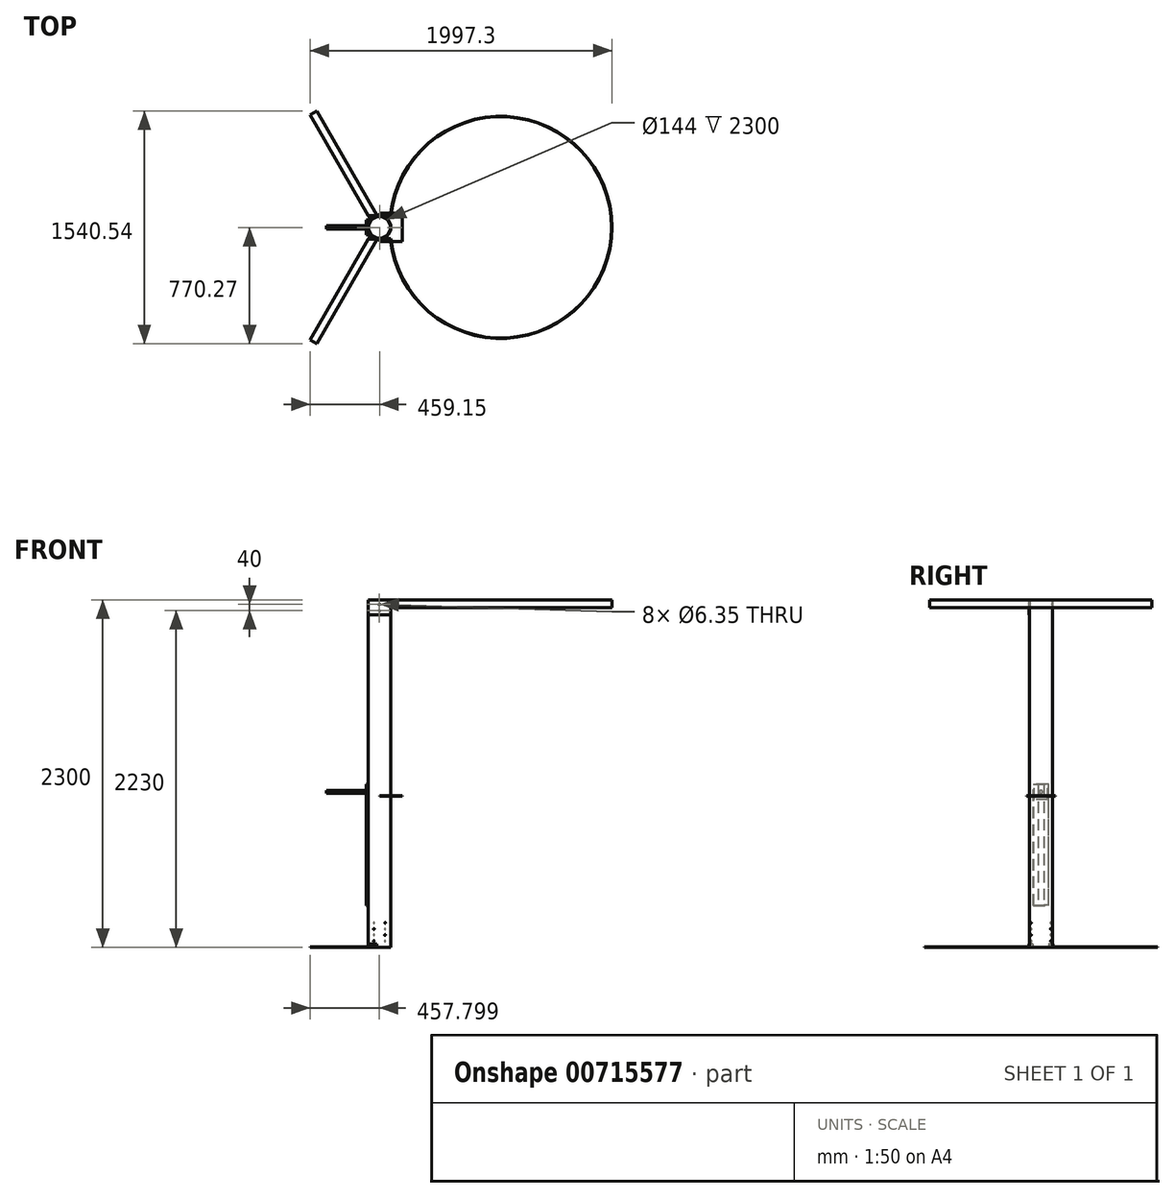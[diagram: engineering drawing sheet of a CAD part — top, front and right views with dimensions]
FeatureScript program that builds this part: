
annotation { "Feature Type Name" : "Feature", "Feature Type Description" : "" }
export const myFeature = defineFeature(function(context is Context, id is Id, definition is map)
    precondition{}
    {
        {
            assignVariable(context, id + "F0", {"name" : "DTubo", "anyValue" : 150 * mm});
        }
        {
            assignVariable(context, id + "F1", {"name" : "hTubo", "anyValue" : 2300 * mm});
        }
        {
            assignVariable(context, id + "F2", {"name" : "tSolera", "anyValue" : 3 * mm});
        }
        {
            assignVariable(context, id + "F3", {"name" : "hProl", "anyValue" : 20});
        }
        {
            assignVariable(context, id + "F4", {"name" : "aSolera", "anyValue" : 50 * mm});
        }
        {
            assignVariable(context, id + "F5", {"name" : "hViga", "anyValue" : 1000 * mm});
        }
        {
            assignVariable(context, id + "F6", {"name" : "hMovil", "anyValue" : 100 * mm});
        }
        {
            var Q0;
            Q0=qCreatedBy(makeId("Top.planeOp"),FACE);
            var sketch = newSketch(context, id + "F7", { "sketchPlane" : qUnion([Q0])});
            skCircle(sketch, "E0", {"center": v(0, 0) * mm, "radius": 72 * mm});
            skCircle(sketch, "E1", {"center": v(0, 0) * mm, "radius": 75 * mm});
            skSolve(sketch);
        }
        {
            var Q0;
            Q0 = qSketchRegion(id + "F7", true);
            extrude(context, id + "F8", {"entities" : qUnion([Q0]), "depth" : getVariable(context, 'hTubo'), "offsetDistance" : 25 * mm});
        }
        {
            var Q0;
            Q0=qCreatedBy(makeId("Top.planeOp"),FACE);
            var sketch = newSketch(context, id + "F9", { "sketchPlane" : qUnion([Q0])});
            skLineSegment(sketch, "E2", {"start": v(0, 0) * mm, "end": v(-521.96, 0) * mm, "construction": true});
            skLineSegment(sketch, "E3", {"start": v(0, 0) * mm, "end": v(-254.09, -440.1) * mm, "construction": true});
            skLineSegment(sketch, "E4", {"start": v(-59.15, -52.45) * mm, "end": v(-15.85, -77.45) * mm});
            skLineSegment(sketch, "E5", {"start": v(-15.85, -77.45) * mm, "end": v(-415.85, -770.27) * mm});
            skLineSegment(sketch, "E6", {"start": v(-415.85, -770.27) * mm, "end": v(-459.15, -745.27) * mm});
            skLineSegment(sketch, "E7", {"start": v(-459.15, -745.27) * mm, "end": v(-59.15, -52.45) * mm});
            skPoint(sketch, "E8", {"position": v(-437.5, -757.77) * mm});
            skLineSegment(sketch, "E9.MirrorCS", {"start": v(-459.15, 745.27) * mm, "end": v(-59.15, 52.45) * mm});
            skLineSegment(sketch, "E10.MirrorCS", {"start": v(0, 0) * mm, "end": v(-254.09, 440.1) * mm, "construction": true});
            skLineSegment(sketch, "E11.MirrorCS", {"start": v(-15.85, 77.45) * mm, "end": v(-415.85, 770.27) * mm});
            skLineSegment(sketch, "E12.MirrorCS", {"start": v(-415.85, 770.27) * mm, "end": v(-459.15, 745.27) * mm});
            skPoint(sketch, "E13.MirrorP", {"position": v(-437.5, 757.77) * mm});
            skLineSegment(sketch, "E14.MirrorCS", {"start": v(-59.15, 52.45) * mm, "end": v(-15.85, 77.45) * mm});
            skSolve(sketch);
        }
        {
            var Q0;
            Q0=makeQuery(id+"F9.imprint","IMPRINT",FACE,{"disambiguationData":[TD([[makeQuery(id+"F9.imprint","IMPRINT",EDGE,{"derivedFrom":sQuery(id+"F9.wireOp",EDGE,"E4")}),-1.0]])]});
            var Q1;
            Q1=makeQuery(id+"F9.imprint","IMPRINT",FACE,{"disambiguationData":[TD([[makeQuery(id+"F9.imprint","IMPRINT",EDGE,{"derivedFrom":sQuery(id+"F9.wireOp",EDGE,"E9.MirrorCS")}),1.0]])]});
            extrude(context, id + "F10", {"entities" : qUnion([Q0, Q1]), "depth" : getVariable(context, 'tSolera'), "offsetDistance" : 25 * mm});
        }
        {
            var Q0;
            Q0=makeQuery(id+"F10.opExtrude","CAP_FACE",FACE,{"disambiguationData":[OSD([sQuery(id+"F9.wireOp",EDGE,"E4"),sQuery(id+"F9.wireOp",EDGE,"E5"),sQuery(id+"F9.wireOp",EDGE,"E6"),sQuery(id+"F9.wireOp",EDGE,"E7")])],"isStart":false});
            var sketch = newSketch(context, id + "F11", { "sketchPlane" : qUnion([Q0])});
            skLineSegment(sketch, "E15", {"start": v(-59.15, -52.45) * mm, "end": v(-15.85, -77.45) * mm});
            skLineSegment(sketch, "E16", {"start": v(-15.85, -77.45) * mm, "end": v(-17.35, -80.05) * mm});
            skLineSegment(sketch, "E17", {"start": v(-17.35, -80.05) * mm, "end": v(-60.65, -55.05) * mm});
            skLineSegment(sketch, "E18", {"start": v(-60.65, -55.05) * mm, "end": v(-59.15, -52.45) * mm});
            skLineSegment(sketch, "E19", {"start": v(-59.15, 52.45) * mm, "end": v(-15.85, 77.45) * mm});
            skLineSegment(sketch, "E20", {"start": v(-15.85, 77.45) * mm, "end": v(-17.35, 80.05) * mm});
            skLineSegment(sketch, "E21", {"start": v(-17.35, 80.05) * mm, "end": v(-60.65, 55.05) * mm});
            skLineSegment(sketch, "E22", {"start": v(-60.65, 55.05) * mm, "end": v(-59.15, 52.45) * mm});
            skSolve(sketch);
        }
        {
            var Q0;
            Q0=makeQuery(id+"F11.imprint","IMPRINT",FACE,{"disambiguationData":[TD([[makeQuery(id+"F11.imprint","IMPRINT",EDGE,{"derivedFrom":sQuery(id+"F11.wireOp",EDGE,"E15")}),-1.0]])]});
            var Q1;
            Q1=makeQuery(id+"F11.imprint","IMPRINT",FACE,{"disambiguationData":[TD([[makeQuery(id+"F11.imprint","IMPRINT",EDGE,{"derivedFrom":sQuery(id+"F11.wireOp",EDGE,"E19")}),1.0]])]});
            extrude(context, id + "F12", {"entities" : qUnion([Q0, Q1]), "operationType" : NewBodyOperationType.ADD, "depth" : (getVariable(context, 'hProl')) * mm, "offsetDistance" : 25 * mm});
        }
        {
            var Q0;
            Q0=makeQuery(id+"F12.opExtrude","SWEPT_FACE",FACE,{"disambiguationData":[OSD([sQuery(id+"F11.wireOp",EDGE,"E17")])]});
            var sketch = newSketch(context, id + "F13", { "sketchPlane" : qUnion([Q0])});
            skLineSegment(sketch, "E23", {"start": v(0, 0) * mm, "end": v(0, 203) * mm, "construction": true});
            skCircle(sketch, "E24", {"center": v(0, 43) * mm, "radius": 3.18 * mm});
            skCircle(sketch, "E25", {"center": v(0, 123) * mm, "radius": 3.18 * mm});
            skSolve(sketch);
        }
        {
            var Q0;
            Q0 = qSketchRegion(id + "F13", true);
            extrude(context, id + "F14", {"entities" : qUnion([Q0]), "operationType" : NewBodyOperationType.REMOVE, "endBound" : BoundingType.THROUGH_ALL, "oppositeDirection" : true, "depth" : 25 * mm, "offsetDistance" : 25 * mm});
        }
        {
            var Q0;
            Q0=makeQuery(id+"F12.opExtrude","SWEPT_FACE",FACE,{"disambiguationData":[OSD([sQuery(id+"F11.wireOp",EDGE,"E21")])]});
            var sketch = newSketch(context, id + "F15", { "sketchPlane" : qUnion([Q0])});
            skLineSegment(sketch, "E26", {"start": v(0, 0) * mm, "end": v(0, 203) * mm, "construction": true});
            skCircle(sketch, "E27", {"center": v(0, 83) * mm, "radius": 3.18 * mm});
            skCircle(sketch, "E28", {"center": v(0, 163) * mm, "radius": 3.18 * mm});
            skSolve(sketch);
        }
        {
            var Q0;
            Q0 = qSketchRegion(id + "F15", true);
            extrude(context, id + "F16", {"entities" : qUnion([Q0]), "operationType" : NewBodyOperationType.REMOVE, "endBound" : BoundingType.THROUGH_ALL, "oppositeDirection" : true, "depth" : 25 * mm, "offsetDistance" : 25 * mm});
        }
        {
            var Q0;
            Q0=makeQuery(id+"F8.opExtrude","CAP_FACE",FACE,{"disambiguationData":[OSD([sQuery(id+"F7.wireOp",EDGE,"E0"),sQuery(id+"F7.wireOp",EDGE,"E1")])],"isStart":false});
            var sketch = newSketch(context, id + "F17", { "sketchPlane" : qUnion([Q0])});
            skLineSegment(sketch, "E29", {"start": v(-75, 75) * mm, "end": v(75, 75) * mm});
            skLineSegment(sketch, "E30", {"start": v(-75, -75) * mm, "end": v(75, -75) * mm});
            skLineSegment(sketch, "E31", {"start": v(75, -75) * mm, "end": v(75, 75) * mm, "construction": true});
            skArc(sketch, "E32", {"start": v(75, -75) * mm, "mid": v(1535.15, 0) * mm, "end": v(75, 75) * mm});
            skLineSegment(sketch, "E33", {"start": v(-75, 75) * mm, "end": v(-75, -75) * mm, "construction": true});
            skArc(sketch, "E34", {"start": v(72.3, -78) * mm, "mid": v(1538.15, 0) * mm, "end": v(72.3, 78) * mm});
            skLineSegment(sketch, "E35", {"start": v(-75, 75) * mm, "end": v(-75, 78) * mm});
            skLineSegment(sketch, "E36", {"start": v(-75, 78) * mm, "end": v(72.3, 78) * mm});
            skLineSegment(sketch, "E37", {"start": v(-75, -75) * mm, "end": v(-75, -78) * mm});
            skLineSegment(sketch, "E38", {"start": v(-75, -78) * mm, "end": v(72.3, -78) * mm});
            skSolve(sketch);
        }
        {
            var Q0;
            Q0 = qSketchRegion(id + "F17", true);
            extrude(context, id + "F18", {"entities" : qUnion([Q0]), "operationType" : NewBodyOperationType.ADD, "oppositeDirection" : true, "depth" : getVariable(context, 'aSolera'), "offsetDistance" : 25 * mm});
        }
        {
            var Q0;
            Q0=makeQuery(id+"F18.opExtrude","CAP_FACE",FACE,{"disambiguationData":[OSD([sQuery(id+"F17.wireOp",EDGE,"E29"),sQuery(id+"F17.wireOp",EDGE,"E30"),sQuery(id+"F17.wireOp",EDGE,"E32"),sQuery(id+"F17.wireOp",EDGE,"E34"),sQuery(id+"F17.wireOp",EDGE,"E35"),sQuery(id+"F17.wireOp",EDGE,"E36"),sQuery(id+"F17.wireOp",EDGE,"E37"),sQuery(id+"F17.wireOp",EDGE,"E38")])],"isStart":false});
            var sketch = newSketch(context, id + "F19", { "sketchPlane" : qUnion([Q0])});
            skLineSegment(sketch, "E39.bottom", {"start": v(-75, 78) * mm, "end": v(75, 78) * mm});
            skLineSegment(sketch, "E39.top", {"start": v(-75, 75) * mm, "end": v(75, 75) * mm});
            skLineSegment(sketch, "E39.left", {"start": v(-75, 78) * mm, "end": v(-75, 75) * mm});
            skLineSegment(sketch, "E39.right", {"start": v(75, 78) * mm, "end": v(75, 75) * mm});
            skLineSegment(sketch, "E40.bottom", {"start": v(-75, -78) * mm, "end": v(75, -78) * mm});
            skLineSegment(sketch, "E40.top", {"start": v(-75, -75) * mm, "end": v(75, -75) * mm});
            skLineSegment(sketch, "E40.left", {"start": v(-75, -78) * mm, "end": v(-75, -75) * mm});
            skLineSegment(sketch, "E40.right", {"start": v(75, -78) * mm, "end": v(75, -75) * mm});
            skSolve(sketch);
        }
        {
            var Q0;
            Q0 = qSketchRegion(id + "F19", true);
            extrude(context, id + "F20", {"entities" : qUnion([Q0]), "operationType" : NewBodyOperationType.ADD, "depth" : 50 * mm, "offsetDistance" : 25 * mm});
        }
        {
            var Q0;
            Q0=qCreatedBy(makeId("Top.planeOp"),FACE);
            cPlane(context, id + "F21", {"entities" : qUnion([Q0]), "cplaneType" : CPlaneType.OFFSET, "offset" : getVariable(context, 'hViga'), "width" : 150 * mm, "height" : 150 * mm});
        }
        {
            var Q0;
            Q0=qCreatedBy(id+"F21.planeOp",FACE);
            var sketch = newSketch(context, id + "F22", { "sketchPlane" : qUnion([Q0])});
            skArc(sketch, "E41", {"start": v(0, -75) * mm, "mid": v(75, 0) * mm, "end": v(0, 75) * mm});
            skLineSegment(sketch, "E42", {"start": v(0, -75) * mm, "end": v(0, 75) * mm, "construction": true});
            skLineSegment(sketch, "E43", {"start": v(0, 75) * mm, "end": v(0, 95) * mm});
            skLineSegment(sketch, "E44", {"start": v(0, 95) * mm, "end": v(150, 95) * mm});
            skLineSegment(sketch, "E45", {"start": v(150, 95) * mm, "end": v(150, -95) * mm});
            skLineSegment(sketch, "E46", {"start": v(150, -95) * mm, "end": v(0, -95) * mm});
            skLineSegment(sketch, "E47", {"start": v(0, -95) * mm, "end": v(0, -75) * mm});
            skSolve(sketch);
        }
        {
            var Q0;
            Q0 = qSketchRegion(id + "F22", true);
            extrude(context, id + "F23", {"entities" : qUnion([Q0]), "operationType" : NewBodyOperationType.ADD, "depth" : getVariable(context, 'tSolera'), "offsetDistance" : 25 * mm});
        }
        {
            var Q0;
            Q0=qCreatedBy(makeId("Right.planeOp"),FACE);
            cPlane(context, id + "F24", {"entities" : qUnion([Q0]), "cplaneType" : CPlaneType.OFFSET, "offset" : getVariable(context, 'DTubo') / 2, "oppositeDirection" : true, "width" : 150 * mm, "height" : 150 * mm});
        }
        {
            var Q0;
            Q0=qCreatedBy(id+"F24.planeOp",FACE);
            var sketch = newSketch(context, id + "F25", { "sketchPlane" : qUnion([Q0])});
            skLineSegment(sketch, "E48.bottom", {"start": v(-50, 280) * mm, "end": v(50, 280) * mm});
            skLineSegment(sketch, "E48.top", {"start": v(-50, 1080) * mm, "end": v(50, 1080) * mm});
            skLineSegment(sketch, "E48.left", {"start": v(-50, 280) * mm, "end": v(-50, 1080) * mm});
            skLineSegment(sketch, "E48.right", {"start": v(50, 280) * mm, "end": v(50, 1080) * mm});
            skPoint(sketch, "E48.middle", {"position": v(0, 680) * mm});
            skLineSegment(sketch, "E49", {"start": v(-50, 330) * mm, "end": v(50, 330) * mm, "construction": true});
            skSolve(sketch);
        }
        {
            var Q0;
            Q0 = qSketchRegion(id + "F25", true);
            extrude(context, id + "F26", {"entities" : qUnion([Q0]), "oppositeDirection" : true, "depth" : getVariable(context, 'tSolera'), "offsetDistance" : 25 * mm});
        }
        {
            var Q0;
            Q0=makeQuery(id+"F26.opExtrude","CAP_FACE",FACE,{"disambiguationData":[OSD([sQuery(id+"F25.wireOp",EDGE,"E48.bottom"),sQuery(id+"F25.wireOp",EDGE,"E48.top"),sQuery(id+"F25.wireOp",EDGE,"E48.left"),sQuery(id+"F25.wireOp",EDGE,"E48.right")])],"isStart":false});
            var sketch = newSketch(context, id + "F27", { "sketchPlane" : qUnion([Q0])});
            skLineSegment(sketch, "E50.bottom", {"start": v(-50, 1080) * mm, "end": v(-47, 1080) * mm});
            skLineSegment(sketch, "E50.top", {"start": v(-50, 280) * mm, "end": v(-47, 280) * mm});
            skLineSegment(sketch, "E50.left", {"start": v(-50, 1080) * mm, "end": v(-50, 280) * mm});
            skLineSegment(sketch, "E50.right", {"start": v(-47, 1080) * mm, "end": v(-47, 280) * mm});
            skLineSegment(sketch, "E51.bottom", {"start": v(50, 280) * mm, "end": v(47, 280) * mm});
            skLineSegment(sketch, "E51.top", {"start": v(50, 1080) * mm, "end": v(47, 1080) * mm});
            skLineSegment(sketch, "E51.left", {"start": v(50, 280) * mm, "end": v(50, 1080) * mm});
            skLineSegment(sketch, "E51.right", {"start": v(47, 280) * mm, "end": v(47, 1080) * mm});
            skSolve(sketch);
        }
        {
            var Q0;
            Q0 = qSketchRegion(id + "F27", true);
            extrude(context, id + "F28", {"entities" : qUnion([Q0]), "operationType" : NewBodyOperationType.ADD, "depth" : 5 * mm, "offsetDistance" : 25 * mm});
        }
        {
            var Q0;
            Q0=makeQuery(id+"F28.opExtrude","CAP_FACE",FACE,{"disambiguationData":[OSD([sQuery(id+"F27.wireOp",EDGE,"E51.bottom"),sQuery(id+"F27.wireOp",EDGE,"E51.top"),sQuery(id+"F27.wireOp",EDGE,"E51.left"),sQuery(id+"F27.wireOp",EDGE,"E51.right")])],"isStart":false});
            var sketch = newSketch(context, id + "F29", { "sketchPlane" : qUnion([Q0])});
            skLineSegment(sketch, "E52.bottom", {"start": v(50, 1080) * mm, "end": v(20, 1080) * mm});
            skLineSegment(sketch, "E52.top", {"start": v(50, 280) * mm, "end": v(20, 280) * mm});
            skLineSegment(sketch, "E52.left", {"start": v(50, 1080) * mm, "end": v(50, 280) * mm});
            skLineSegment(sketch, "E52.right", {"start": v(20, 1080) * mm, "end": v(20, 280) * mm});
            skLineSegment(sketch, "E53.bottom", {"start": v(-50, 1080) * mm, "end": v(-20, 1080) * mm});
            skLineSegment(sketch, "E53.top", {"start": v(-50, 280) * mm, "end": v(-20, 280) * mm});
            skLineSegment(sketch, "E53.left", {"start": v(-50, 1080) * mm, "end": v(-50, 280) * mm});
            skLineSegment(sketch, "E53.right", {"start": v(-20, 1080) * mm, "end": v(-20, 280) * mm});
            skSolve(sketch);
        }
        {
            var Q0;
            Q0 = qSketchRegion(id + "F29", true);
            extrude(context, id + "F30", {"entities" : qUnion([Q0]), "operationType" : NewBodyOperationType.ADD, "depth" : getVariable(context, 'tSolera'), "offsetDistance" : 25 * mm});
        }
        {
            var Q0;
            Q0=makeQuery(id+"F30.boolean.opBoolean","MERGE",FACE,{"derivedFrom":[makeQuery(id+"F28.boolean.opBoolean","MERGE",FACE,{"derivedFrom":[makeQuery(id+"F26.opExtrude","SWEPT_FACE",FACE,{"disambiguationData":[OSD([sQuery(id+"F25.wireOp",EDGE,"E48.bottom")])]}),makeQuery(id+"F28.opExtrude","SWEPT_FACE",FACE,{"disambiguationData":[OSD([sQuery(id+"F27.wireOp",EDGE,"E50.top")])]}),makeQuery(id+"F28.opExtrude","SWEPT_FACE",FACE,{"disambiguationData":[OSD([sQuery(id+"F27.wireOp",EDGE,"E51.bottom")])]})]}),makeQuery(id+"F30.opExtrude","SWEPT_FACE",FACE,{"disambiguationData":[OSD([sQuery(id+"F29.wireOp",EDGE,"E52.top")])]}),makeQuery(id+"F30.opExtrude","SWEPT_FACE",FACE,{"disambiguationData":[OSD([sQuery(id+"F29.wireOp",EDGE,"E53.top")])]})]});
            var sketch = newSketch(context, id + "F31", { "sketchPlane" : qUnion([Q0])});
            skLineSegment(sketch, "E54.bottom", {"start": v(-86, -50) * mm, "end": v(-75, -50) * mm});
            skLineSegment(sketch, "E54.top", {"start": v(-86, 50) * mm, "end": v(-75, 50) * mm});
            skLineSegment(sketch, "E54.left", {"start": v(-86, -50) * mm, "end": v(-86, 50) * mm});
            skLineSegment(sketch, "E54.right", {"start": v(-75, -50) * mm, "end": v(-75, 50) * mm});
            skSolve(sketch);
        }
        {
            var Q0;
            Q0 = qSketchRegion(id + "F31", true);
            extrude(context, id + "F32", {"entities" : qUnion([Q0]), "depth" : getVariable(context, 'tSolera'), "offsetDistance" : 25 * mm});
        }
        {
            var Q0;
            Q0=makeQuery(id+"F30.boolean.opBoolean","MERGE",FACE,{"derivedFrom":[makeQuery(id+"F28.boolean.opBoolean","MERGE",FACE,{"derivedFrom":[makeQuery(id+"F26.opExtrude","SWEPT_FACE",FACE,{"disambiguationData":[OSD([sQuery(id+"F25.wireOp",EDGE,"E48.top")])]}),makeQuery(id+"F28.opExtrude","SWEPT_FACE",FACE,{"disambiguationData":[OSD([sQuery(id+"F27.wireOp",EDGE,"E50.bottom")])]}),makeQuery(id+"F28.opExtrude","SWEPT_FACE",FACE,{"disambiguationData":[OSD([sQuery(id+"F27.wireOp",EDGE,"E51.top")])]})]}),makeQuery(id+"F30.opExtrude","SWEPT_FACE",FACE,{"disambiguationData":[OSD([sQuery(id+"F29.wireOp",EDGE,"E52.bottom")])]}),makeQuery(id+"F30.opExtrude","SWEPT_FACE",FACE,{"disambiguationData":[OSD([sQuery(id+"F29.wireOp",EDGE,"E53.bottom")])]})]});
            var sketch = newSketch(context, id + "F33", { "sketchPlane" : qUnion([Q0])});
            skLineSegment(sketch, "E55.bottom", {"start": v(-81.7, 44) * mm, "end": v(-78.7, 44) * mm});
            skLineSegment(sketch, "E55.top", {"start": v(-81.7, -44) * mm, "end": v(-78.7, -44) * mm});
            skLineSegment(sketch, "E55.left", {"start": v(-81.7, 44) * mm, "end": v(-81.7, -44) * mm});
            skLineSegment(sketch, "E55.right", {"start": v(-78.7, 44) * mm, "end": v(-78.7, -44) * mm});
            skSolve(sketch);
        }
        {
            var Q0;
            Q0 = qSketchRegion(id + "F33", true);
            extrude(context, id + "F34", {"entities" : qUnion([Q0]), "oppositeDirection" : true, "depth" : getVariable(context, 'hMovil'), "offsetDistance" : 25 * mm});
        }
        {
            var Q0;
            Q0=makeQuery(id+"F34.opExtrude","SWEPT_FACE",FACE,{"disambiguationData":[OSD([sQuery(id+"F33.wireOp",EDGE,"E55.left")])]});
            var sketch = newSketch(context, id + "F35", { "sketchPlane" : qUnion([Q0])});
            skLineSegment(sketch, "E56", {"start": v(-44, 980) * mm, "end": v(44, 1080) * mm, "construction": true});
            skPoint(sketch, "E57", {"position": v(0, 1030) * mm});
            skCircle(sketch, "E58", {"center": v(0, 1030) * mm, "radius": 10 * mm});
            skSolve(sketch);
        }
        {
            var Q0;
            Q0 = qSketchRegion(id + "F35", true);
            extrude(context, id + "F36", {"entities" : qUnion([Q0]), "operationType" : NewBodyOperationType.ADD, "depth" : 270 * mm, "offsetDistance" : 25 * mm});
        }
        {
            var Q0;
            Q0=makeQuery(id+"F20.boolean.opBoolean","MERGE",FACE,{"derivedFrom":[makeQuery(id+"F18.opExtrude","SWEPT_FACE",FACE,{"disambiguationData":[OSD([sQuery(id+"F17.wireOp",EDGE,"E38")])]}),makeQuery(id+"F20.opExtrude","SWEPT_FACE",FACE,{"disambiguationData":[OSD([sQuery(id+"F19.wireOp",EDGE,"E39.bottom")])]})]});
            var sketch = newSketch(context, id + "F37", { "sketchPlane" : qUnion([Q0])});
            skLineSegment(sketch, "E59", {"start": v(-1.35, 2300) * mm, "end": v(-1.35, 2200) * mm, "construction": true});
            skPoint(sketch, "E59.endSnap0", {"position": v(-1.35, 2300) * mm});
            skCircle(sketch, "E60", {"center": v(-1.35, 2270) * mm, "radius": 3.18 * mm});
            skCircle(sketch, "E61", {"center": v(-1.35, 2230) * mm, "radius": 3.18 * mm});
            skSolve(sketch);
        }
        {
            var Q0;
            Q0 = qSketchRegion(id + "F37", true);
            extrude(context, id + "F38", {"entities" : qUnion([Q0]), "operationType" : NewBodyOperationType.REMOVE, "endBound" : BoundingType.THROUGH_ALL, "oppositeDirection" : true, "depth" : 25 * mm, "offsetDistance" : 25 * mm});
        }
    });
